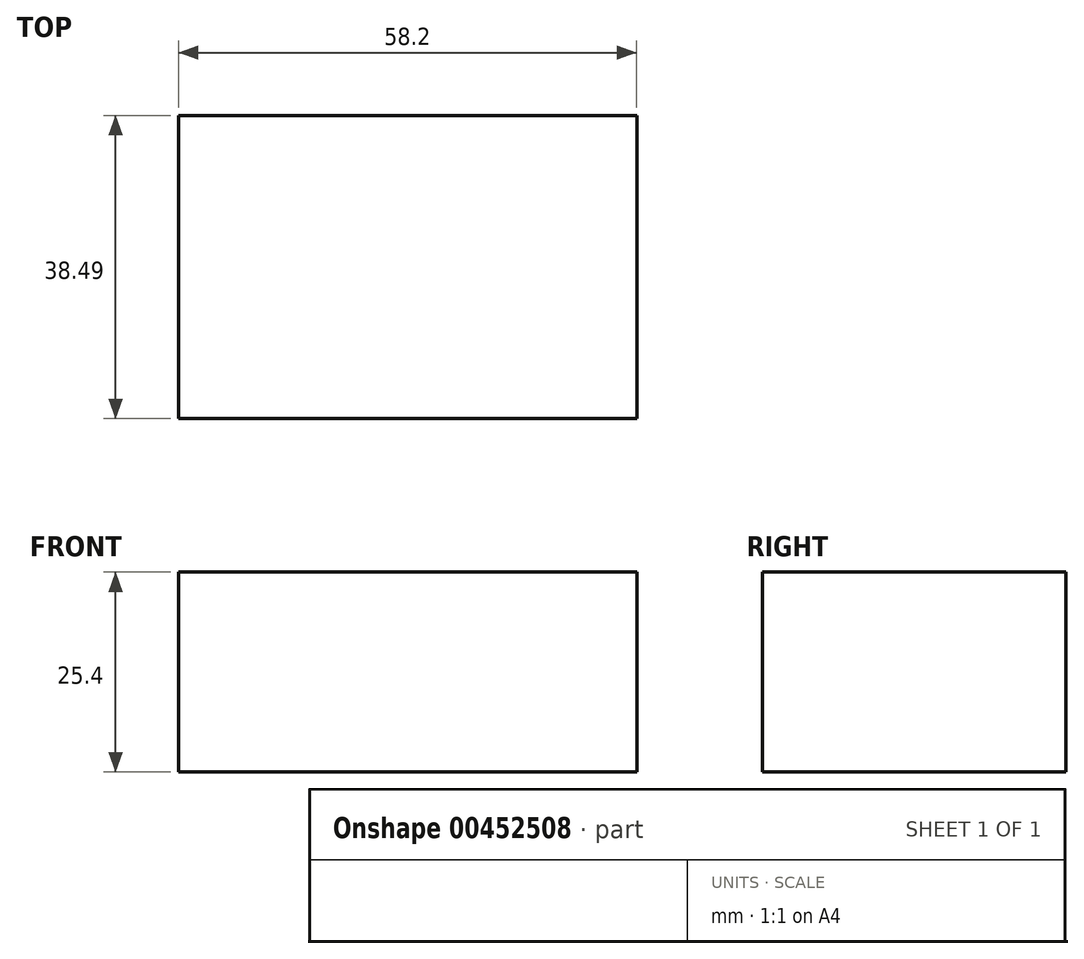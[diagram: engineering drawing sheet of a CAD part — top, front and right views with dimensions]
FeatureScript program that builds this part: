
annotation { "Feature Type Name" : "Feature", "Feature Type Description" : "" }
export const myFeature = defineFeature(function(context is Context, id is Id, definition is map)
    precondition{}
    {
        {
            var Q0;
            Q0=qCreatedBy(makeId("Top.planeOp"),FACE);
            var sketch = newSketch(context, id + "F0", { "sketchPlane" : qUnion([Q0])});
            skLineSegment(sketch, "E0.bottom", {"start": v(1.33, 0) * mm, "end": v(59.53, 0) * mm});
            skLineSegment(sketch, "E0.top", {"start": v(1.33, 38.49) * mm, "end": v(59.53, 38.49) * mm});
            skLineSegment(sketch, "E0.left", {"start": v(1.33, 0) * mm, "end": v(1.33, 38.49) * mm});
            skLineSegment(sketch, "E0.right", {"start": v(59.53, 0) * mm, "end": v(59.53, 38.49) * mm});
            skSolve(sketch);
        }
        {
            var Q0;
            Q0 = qSketchRegion(id + "F0", true);
            extrude(context, id + "F1", {"entities" : qUnion([Q0]), "depth" : 25.4 * mm});
        }
    });
